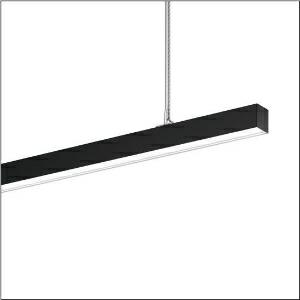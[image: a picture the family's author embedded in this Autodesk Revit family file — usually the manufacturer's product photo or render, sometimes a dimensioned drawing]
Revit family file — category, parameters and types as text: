
# Revit family: silica_r__21_51mx33dn3bbb_5b79
name_source: partatom
category: Lighting Fixtures
units: mm (PartAtom-declared; Revit-internal decimal feet)

## family parameters
Cut with Voids When Loaded = No
Host = Face
Light Source = No
Part Type = Normal
Room Calculation Point = No
Round Connector Dimension = Use Diameter
Shared = No

## types (1)
- --- (1 x LED, 13300 lm, 89.3 W, 3000K)
    Apparent Load = 89 VA
    CIE Flux Codes = 78 96 99 55 100
    Color Rendering = 80
    Color Temperature = 3000K
    Default Elevation = 1800 mm
    Description = Silica® 21, office luminaire, primary optical cover: prismatic diffuser, of PMMA, CAT 2 (L<= 3000cd/m²), light emission: direct/indirect distribution, primary light characteristic: symmetric, installation type: suspended mounting, LED, rated luminous flux: 13.300lm, luminous efficacy: 149lm/W, light colour: 830, colour temperature: 3000K, control gear: DALI 2, with terminal, 3+2-pole, max. 2.5mm², mains connection: 220..240V, AC, 50/60Hz, rated input power: 89.3W, luminaire housing, of aluminium, matt jet black (RAL 9005), length: 2.700mm, width: 53mm, height: 53mm, protection rating (complete): IP20, insulation class (complete): insulation class I (protective earthing), certification: CE, permissible operating ambient temperature: 0..+35°C, standard: EN 50419, packaging unit: 1 piece
    Height = 53 mm
    Lamp = 1 x LED
    Lamp Light Flux = 13300 lm
    Lamp Power = 89.3 W
    Lamp count = 1
    Length = 2704 mm
    Luminous efficacy = 149 lm/W
    Manufacturer = Siteco
    ModVariant = No
    Model = 51MX33DN3BBB
    Mounting Place = Ceiling
    Mounting Type = Pendant
    Number of Poles = 1
    OnlyDefault = Yes
    Power Factor = 1
    Product Name = Silica® 21
    Product group = office luminaire | ceiling pendant
    ProductGroupID = 903
    Protection Class = Protection class I
    Protection Degree = IP 20
    RLX_Detail_Level = 1
    RLX_Emergency_Light_Flux = 0 lm
    RLX_Emergency_Type = 0
    RLX_Emergency_Type_DB = No
    RlxData = <blob elided: 25069 chars, md5=6b91bc58>
    Socket = socket
    Standby Power = 0 W
    System Light Flux = 13300 lm
    System Power = 89 W
    Type Comments = factory setting: luminous flux: 100 % | dim-lin: 254 | 345 mA
    Type Image = l_1335856.jpg
    URL = http://relux.com
    VarID = @adj_084071
    Voltage = 0 V
    Weight = 0.00 kg
    Width = 53 mm

## geometry (parser evidence)
native form markers: Blend x4, Sweep x11
no freeform markers — native parametric forms only
